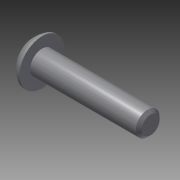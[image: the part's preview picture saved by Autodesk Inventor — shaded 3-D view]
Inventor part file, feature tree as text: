
AUTODESK INVENTOR PART (.ipt)
format: ipt  version: 2015 (Build 190159000, 159)  size: 123,392 bytes
history: native  units: in
note: dims shown in document units (in); Inventor stores cm internally (conversion verified against a paired STEP export)
features: other x2, extrude x1, chamfer x1, imported_body x1, sketch x1
ambient origin geometry x8: Origin, YZ Plane, XZ Plane, XY Plane, X Axis, Y Axis, Z Axis, Center Point
bodies: Body1 (feature_tree)
feature tree (6):
  parser-record x1  (decoder bookkeeping rows leaked as tree rows — omitted from the tree; the rows remain in map.json)
  other  "Bolt"
  extrude  "thread length"  Depth=0.75in TaperAngle=0.0deg
  chamfer  "thread chamfer"  Distance=0.02in Angle=45.0deg
  imported_body  "Base1"
  sketch  "Sketch1"  dims[d0=0.164in d1=0.75in d2=0.0in d3=0.02in d4=0.125in d5=45.0deg d7=0.0in d9=0.0in]
